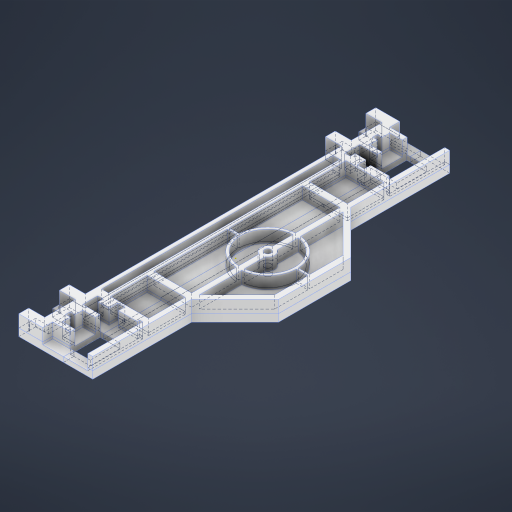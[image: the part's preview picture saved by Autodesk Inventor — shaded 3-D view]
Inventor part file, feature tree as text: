
AUTODESK INVENTOR PART (.ipt)
format: ipt  version: 2024 (Build 280153000, 153)  size: 1,053,696 bytes
history: native  units: mm
features: sketch x27, extrude x25, projected_geometry x8, chamfer x2, other x1
ambient origin geometry x8: Origin, YZ Plane, XZ Plane, XY Plane, X Axis, Y Axis, Z Axis, Center Point
bodies: Body1 (feature_tree)
feature tree (63):
  other  "Твердое тело1"
  extrude  "Выдавливание1"  Depth=722.0mm
  extrude  "Выдавливание2"  Depth=21.0mm
  extrude  "Выдавливание3"  Depth=60.0mm
  extrude  "Выдавливание4"  Depth=10.0mm TaperAngle=0.0deg
  extrude  "Выдавливание5"  Depth=500.0mm
  extrude  "Выдавливание6"  Depth=25.0mm TaperAngle=0.0deg
  extrude  "Выдавливание7"  TaperAngle=0.0deg  [1 undecoded]
  extrude  "Выдавливание8"  Depth=20.0mm
  chamfer  "Фаска1"  Distance=40.0mm
  extrude  "Выдавливание9"  Depth=200.0mm
  extrude  "Выдавливание11"  Depth=42.0mm
  sketch  "Sketch13"  dims[d0=87.0mm d1=722.0mm]
  chamfer  "Chamfer2"  Distance=10.0mm
  extrude  "Extrusion12"  Depth=4.25mm
  extrude  "Extrusion13"  Depth=50.0mm
  extrude  "Extrusion14"  Depth=19.0mm
  extrude  "Extrusion15"  Depth=34.0mm
  extrude  "Extrusion16"  Depth=20.0mm TaperAngle=0.0deg
  extrude  "Extrusion18"  Depth=12.0mm TaperAngle=45.0deg
  extrude  "Extrusion19"  Depth=5.0mm
  extrude  "Extrusion20"  Depth=5.0mm
  sketch  "Sketch22"  dims[d25=200.0mm d26=200.0mm]
  extrude  "Extrusion21"  Depth=19.0mm
  extrude  "Extrusion22"  Depth=19.0mm
  extrude  "Extrusion26"  Depth=2.0mm TaperAngle=0.0deg
  extrude  "Extrusion27"  Depth=10.0mm
  extrude  "Extrusion28"  Depth=20.0mm
  extrude  "Extrusion29"  Depth=5.0mm
  extrude  "Extrusion30"  Depth=25.0mm TaperAngle=0.0deg
  sketch  "Эскиз1"
  sketch  "Эскиз2"
  sketch  "Эскиз3"
  sketch  "Эскиз4"
  sketch  "Эскиз6"
  sketch  "Эскиз7"
  sketch  "Эскиз8"
  sketch  "Эскиз9"
  projected_geometry  "Спроецированная петля1"
  sketch  "Эскиз10"
  projected_geometry  "Спроецированная петля2"
  projected_geometry  "Спроецированная петля3"
  sketch  "Эскиз12"
  sketch  "Sketch14"  dims[d2=10.0mm d3=0.0mm d4=21.0mm]
  sketch  "Sketch15"  dims[d5=16.0mm d6=60.0mm]
  sketch  "Sketch16"  dims[d7=40.0mm d8=10.0mm d9=0.0mm]
  sketch  "Sketch17"  dims[d10=10.0mm d12=500.0mm]
  sketch  "Sketch18"  dims[d13=111.0mm d14=25.0mm d15=0.0mm]
  sketch  "Sketch19"  dims[d16=722.0mm d17=0.0mm]
  sketch  "Sketch20"  dims[d18=35.0mm d19=0.0mm d20=20.0mm]
  sketch  "Sketch21"  dims[d22=10.0mm d23=40.0mm d24=0.0mm]
  projected_geometry  "Projected Loop6"
  sketch  "Sketch23"  dims[d27=5.0mm d28=0.0mm d29=42.0mm]
  projected_geometry  "Projected Loop7"
  sketch  "Sketch24"  dims[d30=70.0mm]
  projected_geometry  "Projected Loop8"
  projected_geometry  "Projected Loop9"
  sketch  "Sketch28"  dims[d31=326.0mm]
  sketch  "Sketch30"  dims[d32=5.0mm]
  sketch  "Sketch31"  dims[d33=10.5mm d34=10.0mm d35=0.0mm]
  sketch  "Sketch32"  dims[d36=4.25mm d37=4.25mm]
  projected_geometry  "Projected Loop10"
  sketch  "Sketch34"  dims[d38=4.25mm d39=4.25mm d40=19.0mm d41=34.0mm d42=20.0mm d43=0.0mm d44=12.0mm d45=2.0mm d46=45.0deg d47=5.0mm d48=5.0mm d49=19.0mm d50=19.0mm d51=2.0mm d52=0.0mm d56=10.0mm d57=20.0mm d58=5.0mm d59=25.0mm d60=0.0mm d61=42.0mm d62=70.0mm d63=5.0mm d64=10.5mm d65=5.0mm d66=5.0mm d67=19.0mm d68=19.0mm d69=19.0mm d70=34.0mm d71=88.0mm d72=2.0mm d73=45.0deg d75=11.0mm d76=40.0mm d77=0.0mm d78=11.0mm d79=11.0mm d80=2.0mm d81=0.0mm d82=10.0mm d83=0.0mm d84=0.0mm d85=0.0mm d86=722.0mm d87=361.0mm d88=21.0mm d89=13.0mm d90=34.0mm d91=32.5mm d92=13.0mm d93=7.0mm d94=5.736667mm d95=5.736897mm d96=15.0mm d97=0.0mm d100=10.0mm d101=0.0mm d102=10.0mm d103=0.0mm d104=20.0mm d105=20.0mm d106=10.0mm d107=10.0mm d108=722.0mm d109=361.0mm d110=30.0mm d111=0.0mm d112=16.0mm d113=16.0mm d114=16.0mm d115=16.0mm d116=5.0mm d117=0.0mm d118=30.0mm d119=0.0mm d131=10.0mm d132=0.0mm d133=0.05mm d134=5.0mm d135=5.0mm d136=1000.0mm d137=0.0mm d138=0.05mm d140=2.0mm d141=1000.0mm d142=0.0mm d143=16.0mm d144=16.0mm d145=8.0mm d146=8.0mm d147=1000.0mm d148=0.0mm d152=110.0mm d153=110.0mm d154=120.0mm d155=50.0mm d156=0.0mm]
note: 1 required parameter value undecoded (feature->parameter linkage not recoverable at this tier; creation-order binding heuristic only, values carry confidence <= 0.55)
